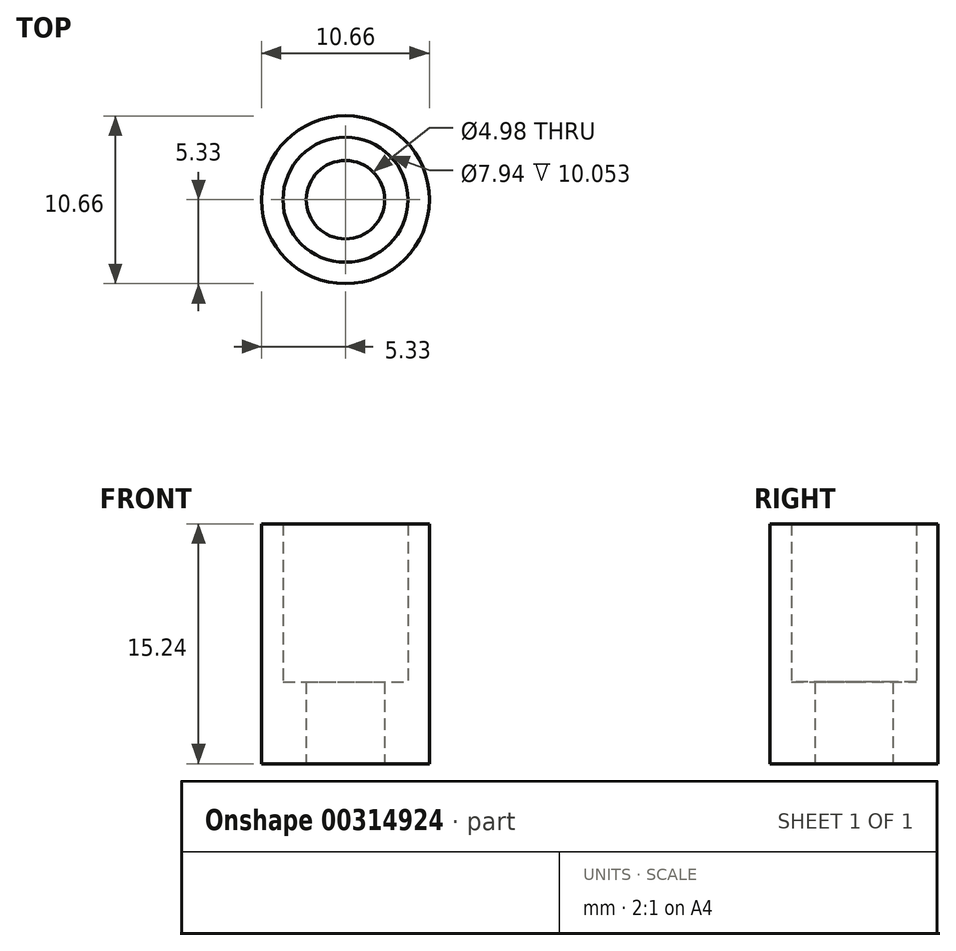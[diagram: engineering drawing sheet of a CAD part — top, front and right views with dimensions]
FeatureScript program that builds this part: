
annotation { "Feature Type Name" : "Feature", "Feature Type Description" : "" }
export const myFeature = defineFeature(function(context is Context, id is Id, definition is map)
    precondition{}
    {
        {
            var Q0;
            Q0=qCreatedBy(makeId("Front.planeOp"),FACE);
            var sketch = newSketch(context, id + "F0", { "sketchPlane" : qUnion([Q0])});
            skLineSegment(sketch, "E0", {"start": v(2.49, 0) * mm, "end": v(5.33, 0) * mm});
            skLineSegment(sketch, "E1", {"start": v(5.33, 0) * mm, "end": v(5.33, 15.24) * mm});
            skLineSegment(sketch, "E2", {"start": v(5.33, 15.24) * mm, "end": v(3.97, 15.24) * mm});
            skLineSegment(sketch, "E3", {"start": v(3.97, 15.24) * mm, "end": v(3.97, 5.19) * mm});
            skLineSegment(sketch, "E4", {"start": v(3.97, 5.19) * mm, "end": v(2.49, 5.19) * mm});
            skLineSegment(sketch, "E5", {"start": v(2.49, 5.19) * mm, "end": v(2.49, 0) * mm});
            skSolve(sketch);
        }
        {
            var Q0;
            Q0=qCreatedBy(makeId("Front.planeOp"),FACE);
            var sketch = newSketch(context, id + "F1", { "sketchPlane" : qUnion([Q0])});
            skLineSegment(sketch, "E6", {"start": v(0, 0) * mm, "end": v(0, 16.6) * mm, "construction": true});
            skSolve(sketch);
        }
        {
            var Q0;
            Q0 = qSketchRegion(id + "F0", true);
            var Q1;
            Q1=sQuery(id+"F1.wireOp",EDGE,"E6");
            revolve(context, id + "F2", {"entities" : qUnion([Q0]), "axis" : qUnion([Q1]), "revolveType" : RevolveType.FULL});
        }
    });
